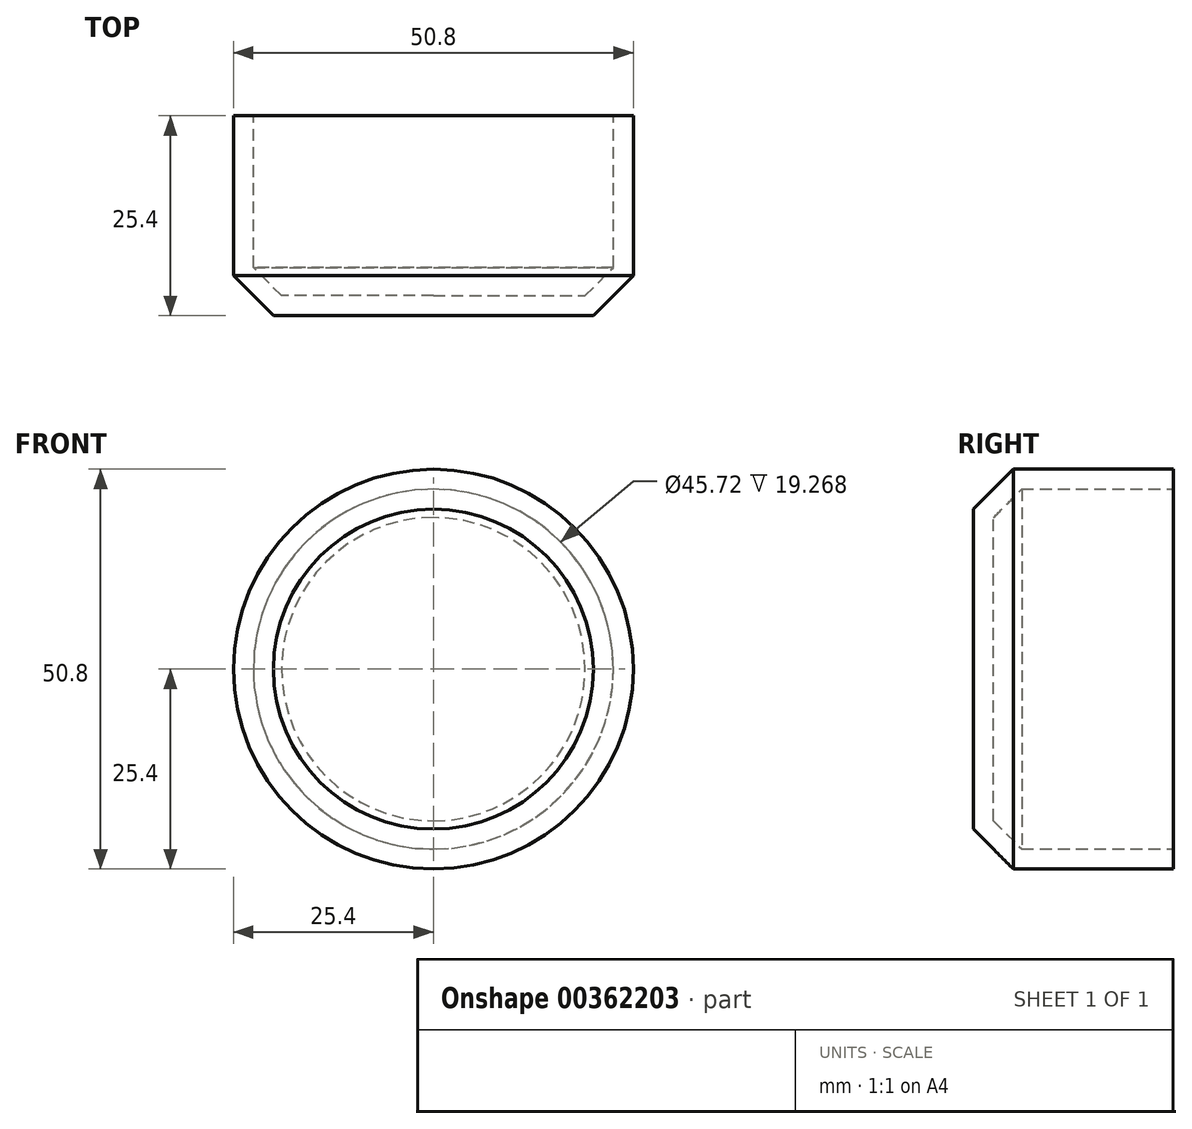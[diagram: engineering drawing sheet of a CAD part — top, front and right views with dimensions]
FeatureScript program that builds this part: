
annotation { "Feature Type Name" : "Feature", "Feature Type Description" : "" }
export const myFeature = defineFeature(function(context is Context, id is Id, definition is map)
    precondition{}
    {
        {
            var Q0;
            Q0=qCreatedBy(makeId("Front.planeOp"),FACE);
            var sketch = newSketch(context, id + "F0", { "sketchPlane" : qUnion([Q0])});
            skCircle(sketch, "E0", {"center": v(0, 0) * mm, "radius": 25.4 * mm});
            skSolve(sketch);
        }
        {
            var Q0;
            Q0 = qSketchRegion(id + "F0", true);
            extrude(context, id + "F1", {"entities" : qUnion([Q0]), "depth" : 25.4 * mm});
        }
        {
            var Q0;
            Q0=makeQuery(id+"F1.opExtrude","CAP_FACE",FACE,{"disambiguationData":[OSD([sQuery(id+"F0.wireOp",EDGE,"E0")])],"isStart":false});
            chamfer(context, id + "F2", {"entities" : qUnion([Q0]), "width" : 5.08 * mm, "tangentPropagation" : true});
        }
        {
            var Q0;
            Q0=makeQuery(id+"F1.opExtrude","CAP_FACE",FACE,{"disambiguationData":[OSD([sQuery(id+"F0.wireOp",EDGE,"E0")])],"isStart":true});
            shell(context, id + "F3", {"entities" : qUnion([Q0]), "thickness" : 2.54 * mm});
        }
    });
